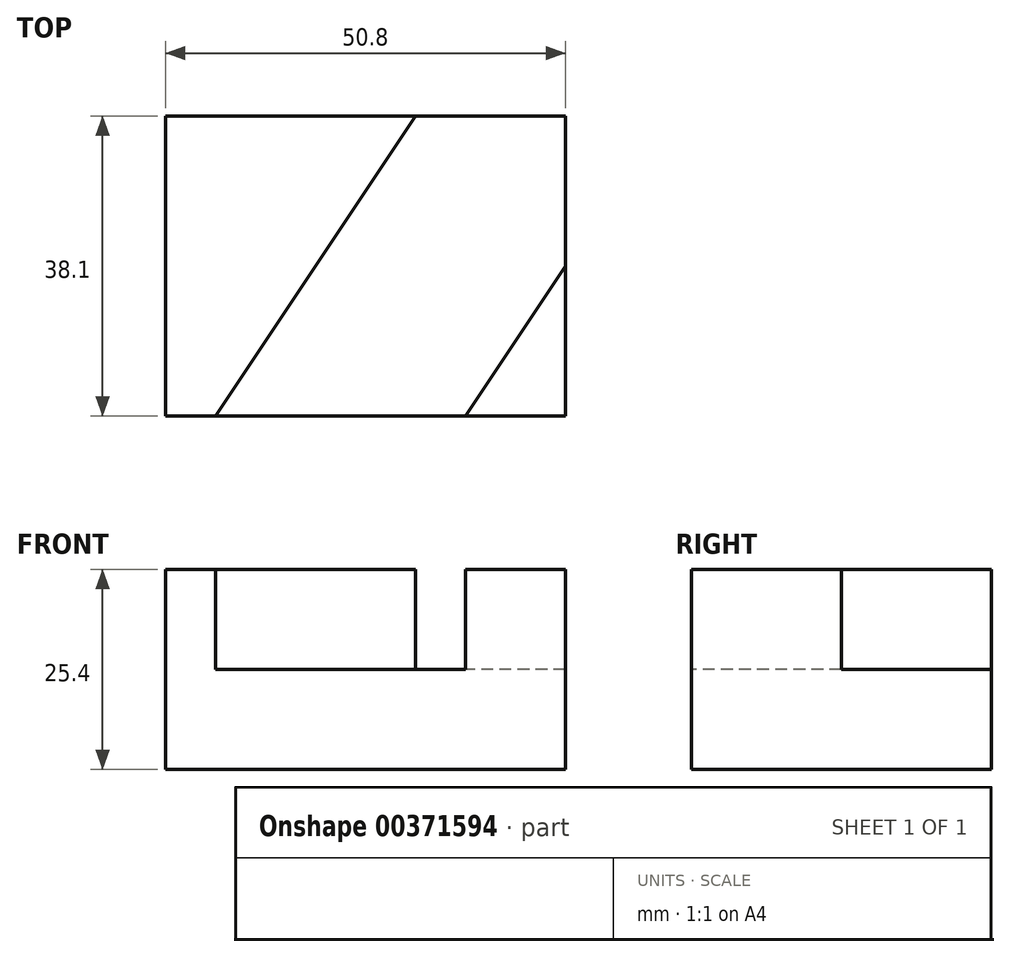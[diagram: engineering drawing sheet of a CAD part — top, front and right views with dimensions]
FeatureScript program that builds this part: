
annotation { "Feature Type Name" : "Feature", "Feature Type Description" : "" }
export const myFeature = defineFeature(function(context is Context, id is Id, definition is map)
    precondition{}
    {
        {
            var Q0;
            Q0=qCreatedBy(makeId("Right.planeOp"),FACE);
            var sketch = newSketch(context, id + "F0", { "sketchPlane" : qUnion([Q0])});
            skLineSegment(sketch, "E0.bottom", {"start": v(0, 0) * mm, "end": v(38.1, 0) * mm});
            skLineSegment(sketch, "E0.top", {"start": v(0, 25.4) * mm, "end": v(38.1, 25.4) * mm});
            skLineSegment(sketch, "E0.left", {"start": v(0, 0) * mm, "end": v(0, 25.4) * mm});
            skLineSegment(sketch, "E0.right", {"start": v(38.1, 0) * mm, "end": v(38.1, 25.4) * mm});
            skSolve(sketch);
        }
        {
            var Q0;
            Q0=makeQuery(id+"F0.imprint","IMPRINT",FACE,{"disambiguationData":[TD([[makeQuery(id+"F0.imprint","IMPRINT",EDGE,{"derivedFrom":sQuery(id+"F0.wireOp",EDGE,"E0.bottom")}),1.0]])]});
            extrude(context, id + "F1", {"entities" : qUnion([Q0]), "depth" : 50.8 * mm});
        }
        {
            var Q0;
            Q0=makeQuery(id+"F1.opExtrude","SWEPT_FACE",FACE,{"disambiguationData":[OSD([sQuery(id+"F0.wireOp",EDGE,"E0.top")])]});
            var sketch = newSketch(context, id + "F2", { "sketchPlane" : qUnion([Q0])});
            skLineSegment(sketch, "E1", {"start": v(50.8, 19.05) * mm, "end": v(38.1, 0) * mm});
            skLineSegment(sketch, "E2", {"start": v(6.35, 0) * mm, "end": v(31.75, 38.1) * mm});
            skSolve(sketch);
        }
        {
            var Q0;
            {var subQ5=sQuery(id+"F2.wireOp",EDGE,"E1");Q0=makeQuery(id+"F2.imprint","IMPRINT",FACE,{"disambiguationData":[TD([[makeQuery(id+"F2.imprint","IMPRINT",EDGE,{"derivedFrom":subQ5}),-1.0]])]});}
            extrude(context, id + "F3", {"entities" : qUnion([Q0]), "operationType" : NewBodyOperationType.REMOVE, "oppositeDirection" : true, "depth" : 12.7 * mm});
        }
    });
